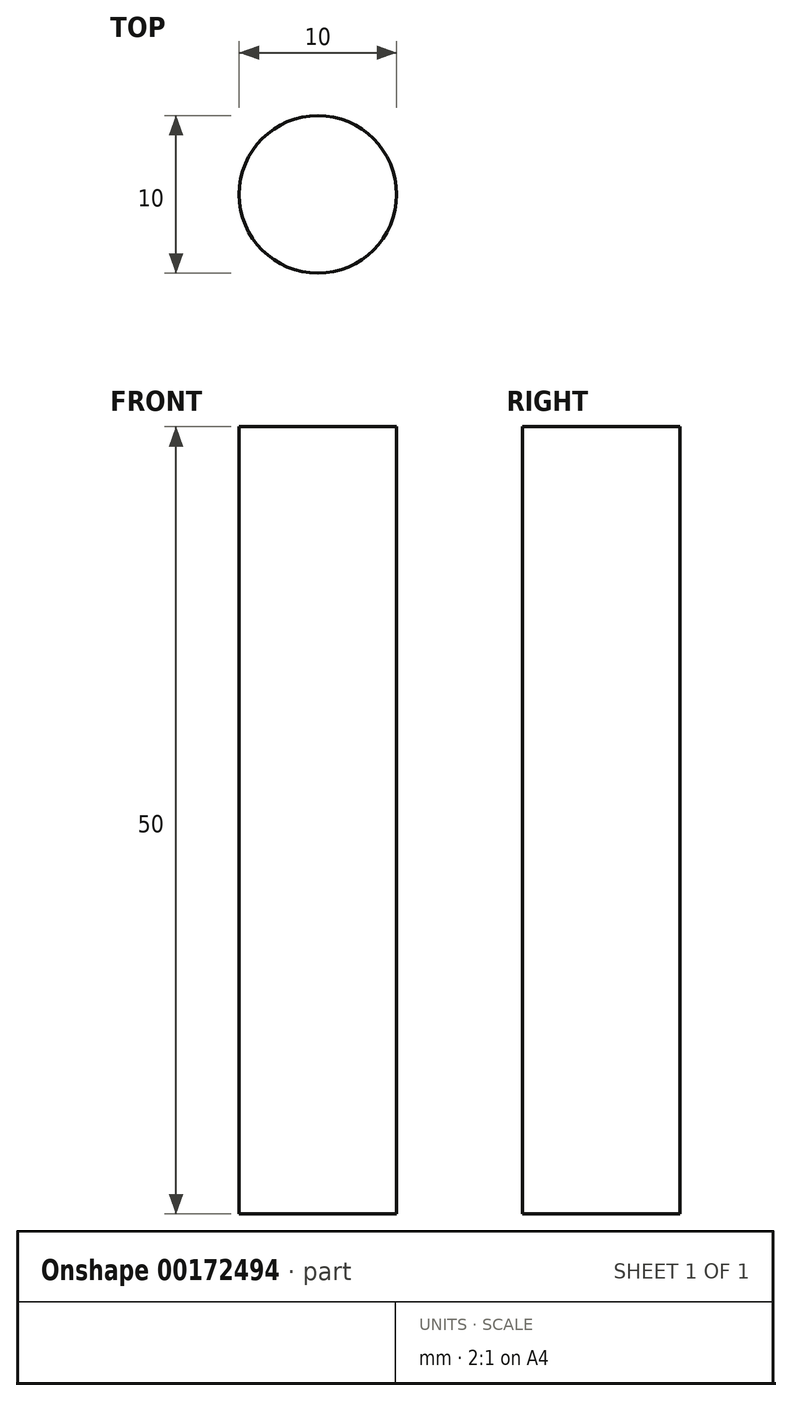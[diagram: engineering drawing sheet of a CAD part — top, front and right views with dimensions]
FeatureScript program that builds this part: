
annotation { "Feature Type Name" : "Feature", "Feature Type Description" : "" }
export const myFeature = defineFeature(function(context is Context, id is Id, definition is map)
    precondition{}
    {
        {
            var Q0;
            Q0=qCreatedBy(makeId("Top.planeOp"),FACE);
            var sketch = newSketch(context, id + "F0", { "sketchPlane" : qUnion([Q0])});
            skCircle(sketch, "E0", {"center": v(0, 0) * mm, "radius": 5 * mm});
            skSolve(sketch);
        }
        {
            var Q0;
            Q0=makeQuery(id+"F0.imprint","IMPRINT",FACE,{"disambiguationData":[TD([[makeQuery(id+"F0.imprint","IMPRINT",EDGE,{"derivedFrom":sQuery(id+"F0.wireOp",EDGE,"E0")}),1.0]])]});
            extrude(context, id + "F1", {"entities" : qUnion([Q0]), "depth" : 50 * mm});
        }
    });
